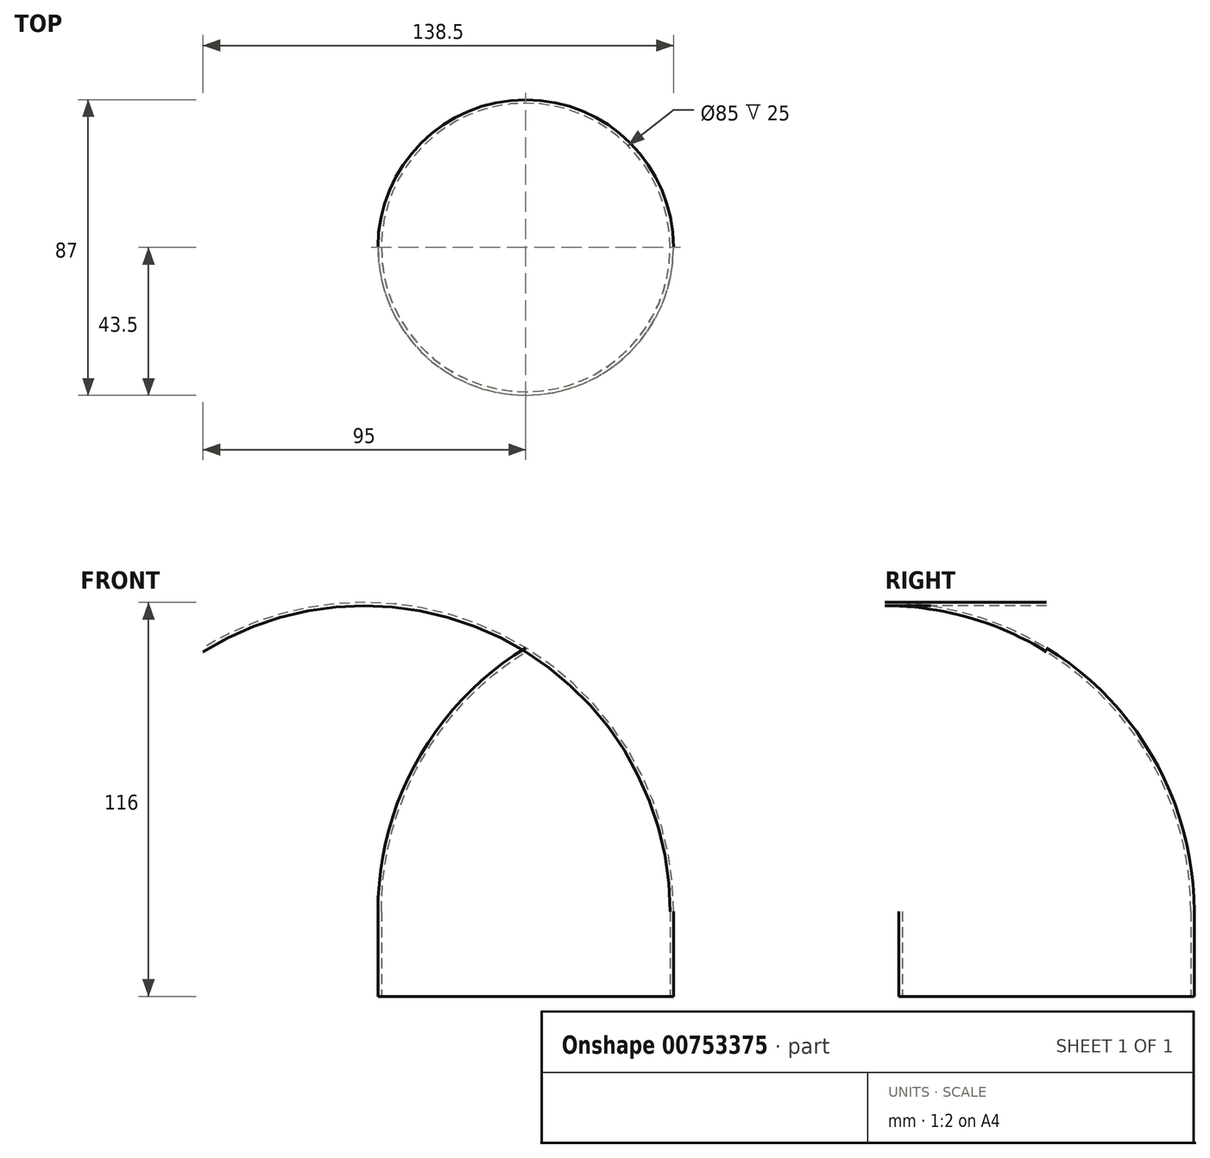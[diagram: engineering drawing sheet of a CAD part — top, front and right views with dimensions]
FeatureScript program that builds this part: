
annotation { "Feature Type Name" : "Feature", "Feature Type Description" : "" }
export const myFeature = defineFeature(function(context is Context, id is Id, definition is map)
    precondition{}
    {
        {
            var Q0;
            Q0=qCreatedBy(makeId("Front.planeOp"),FACE);
            var sketch = newSketch(context, id + "F0", { "sketchPlane" : qUnion([Q0])});
            skLineSegment(sketch, "E0", {"start": v(0, 0) * mm, "end": v(0, 101.44) * mm, "construction": true});
            skArc(sketch, "E1", {"start": v(42.5, 25) * mm, "mid": v(31.16, 68.73) * mm, "end": v(0, 101.44) * mm});
            skLineSegment(sketch, "E2", {"start": v(42.5, 25) * mm, "end": v(42.5, 0) * mm});
            skArc(sketch, "E3.0", {"start": v(43.5, 25) * mm, "mid": v(31.88, 69.49) * mm, "end": v(0, 102.62) * mm});
            skLineSegment(sketch, "E3.1", {"start": v(43.5, 25) * mm, "end": v(43.5, 0) * mm});
            skLineSegment(sketch, "E4", {"start": v(0, 101.44) * mm, "end": v(0, 102.62) * mm});
            skLineSegment(sketch, "E5", {"start": v(42.5, 0) * mm, "end": v(43.5, 0) * mm});
            skSolve(sketch);
        }
        {
            var Q0;
            Q0=qSketchRegion(id+"F0",true);
            var Q1;
            Q1=sQuery(id+"F0.wireOp",EDGE,"E0");
            revolve(context, id + "F1", {"entities" : qUnion([Q0]), "axis" : qUnion([Q1]), "revolveType" : RevolveType.FULL});
        }
    });
